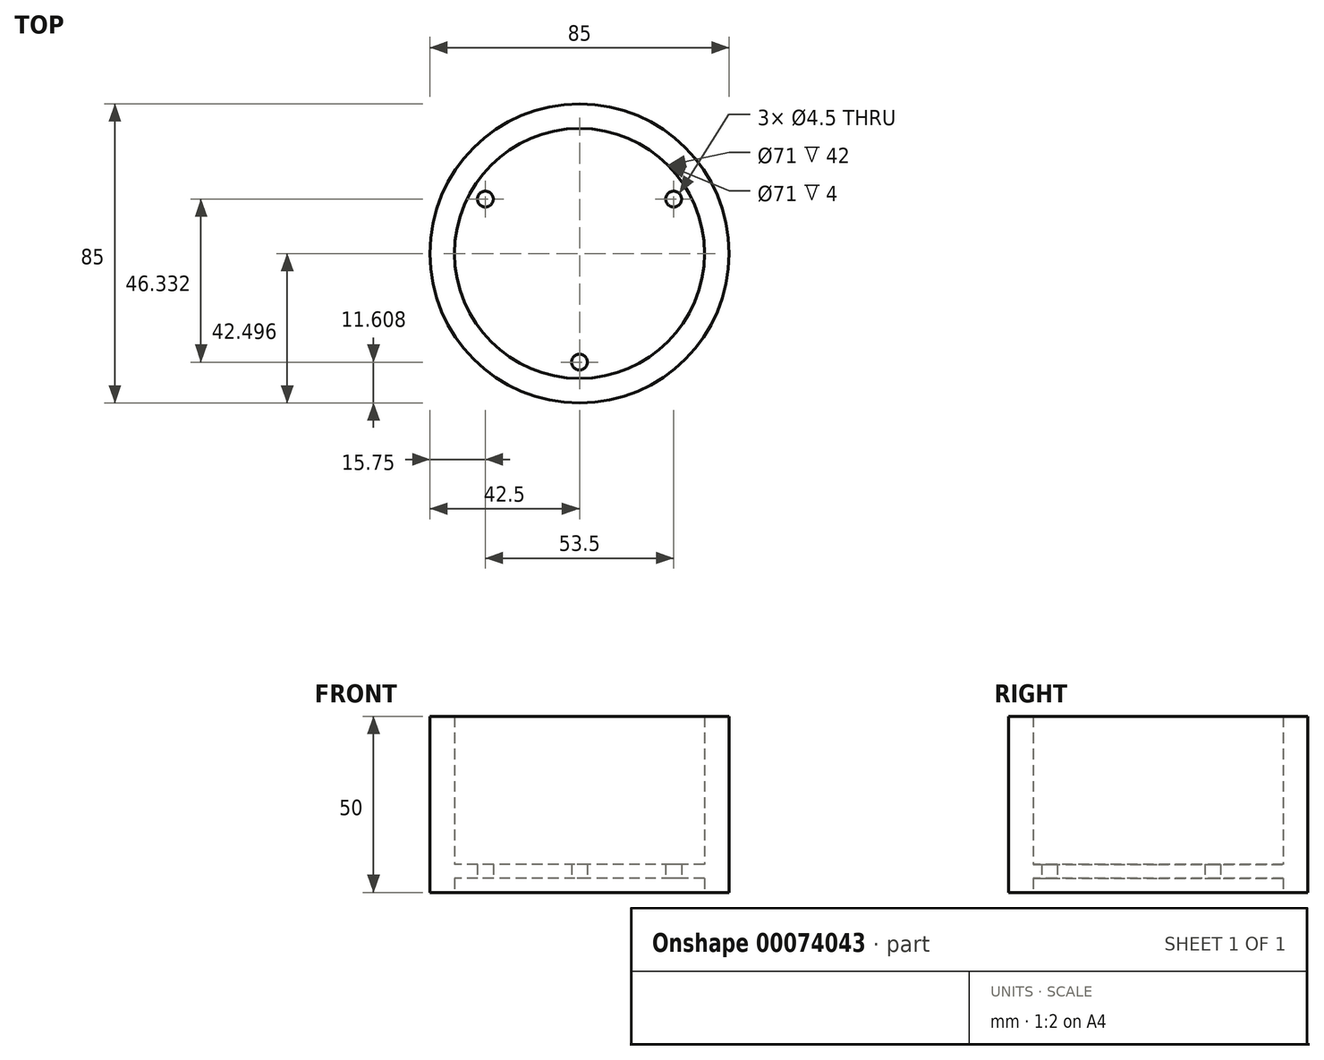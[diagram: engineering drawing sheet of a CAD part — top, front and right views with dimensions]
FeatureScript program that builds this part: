
annotation { "Feature Type Name" : "Feature", "Feature Type Description" : "" }
export const myFeature = defineFeature(function(context is Context, id is Id, definition is map)
    precondition{}
    {
        {
            var Q0;
            Q0=qCreatedBy(makeId("Top.planeOp"),FACE);
            var sketch = newSketch(context, id + "F0", { "sketchPlane" : qUnion([Q0])});
            skLineSegment(sketch, "E0", {"start": v(0, 0) * mm, "end": v(53.5, 0) * mm});
            skLineSegment(sketch, "E1", {"start": v(53.5, 0) * mm, "end": v(26.75, -46.33) * mm});
            skLineSegment(sketch, "E2", {"start": v(26.75, -46.33) * mm, "end": v(0, 0) * mm});
            skLineSegment(sketch, "E3", {"start": v(0, 0) * mm, "end": v(40.12, -23.17) * mm});
            skLineSegment(sketch, "E4", {"start": v(13.38, -23.17) * mm, "end": v(53.5, 0) * mm});
            skLineSegment(sketch, "E5", {"start": v(26.75, -46.33) * mm, "end": v(26.75, 0) * mm});
            skCircle(sketch, "E6", {"center": v(26.75, -15.44) * mm, "radius": 35.5 * mm});
            skCircle(sketch, "E7", {"center": v(26.75, -15.44) * mm, "radius": 42.5 * mm});
            skCircle(sketch, "E8", {"center": v(0, 0) * mm, "radius": 2.25 * mm});
            skCircle(sketch, "E9", {"center": v(53.5, 0) * mm, "radius": 2.25 * mm});
            skCircle(sketch, "E10", {"center": v(26.75, -46.33) * mm, "radius": 2.25 * mm});
            skSolve(sketch);
        }
        {
            var Q0;
            Q0=makeQuery(id+"F0.imprint","IMPRINT",FACE,{"disambiguationData":[TD([[makeQuery(id+"F0.imprint","IMPRINT",EDGE,{"derivedFrom":sQuery(id+"F0.wireOp",EDGE,"E6")}),-1.0]])]});
            var Q1;
            Q1=makeQuery(id+"F0.imprint","IMPRINT",FACE,{"disambiguationData":[TD([[makeQuery(id+"F0.imprint","IMPRINT",EDGE,{"derivedFrom":sQuery(id+"F0.wireOp",EDGE,"E6")}),1.0]])]});
            var Q2;
            {var subQ0=sQuery(id+"F0.wireOp",EDGE,"E4");var subQ1=sQuery(id+"F0.wireOp",EDGE,"E2");var subQ2=makeQuery(id+"F0.imprint","INTERSECT",VERTEX,{"derivedFrom":[subQ1,subQ0]});Q2=makeQuery(id+"F0.imprint","IMPRINT",FACE,{"disambiguationData":[TD([[makeQuery(id+"F0.imprint","IMPRINT",EDGE,{"disambiguationData":[TD([[subQ2,-1.0]])],"derivedFrom":subQ1}),-1.0]])]});}
            var Q3;
            {var subQ0=sQuery(id+"F0.wireOp",EDGE,"E4");var subQ1=sQuery(id+"F0.wireOp",EDGE,"E2");var subQ2=makeQuery(id+"F0.imprint","INTERSECT",VERTEX,{"derivedFrom":[subQ1,subQ0]});Q3=makeQuery(id+"F0.imprint","IMPRINT",FACE,{"disambiguationData":[TD([[makeQuery(id+"F0.imprint","IMPRINT",EDGE,{"disambiguationData":[TD([[subQ2,1.0]])],"derivedFrom":subQ1}),-1.0]])]});}
            var Q4;
            {var subQ0=sQuery(id+"F0.wireOp",EDGE,"E3");var subQ1=sQuery(id+"F0.wireOp",EDGE,"E1");var subQ2=makeQuery(id+"F0.imprint","INTERSECT",VERTEX,{"derivedFrom":[subQ1,subQ0]});Q4=makeQuery(id+"F0.imprint","IMPRINT",FACE,{"disambiguationData":[TD([[makeQuery(id+"F0.imprint","IMPRINT",EDGE,{"disambiguationData":[TD([[subQ2,-1.0]])],"derivedFrom":subQ1}),-1.0]])]});}
            var Q5;
            {var subQ0=sQuery(id+"F0.wireOp",EDGE,"E5");var subQ1=sQuery(id+"F0.wireOp",EDGE,"E0");var subQ2=makeQuery(id+"F0.imprint","INTERSECT",VERTEX,{"derivedFrom":[subQ1,subQ0]});Q5=makeQuery(id+"F0.imprint","IMPRINT",FACE,{"disambiguationData":[TD([[makeQuery(id+"F0.imprint","IMPRINT",EDGE,{"disambiguationData":[TD([[subQ2,1.0]])],"derivedFrom":subQ1}),-1.0]])]});}
            var Q6;
            {var subQ0=sQuery(id+"F0.wireOp",EDGE,"E3");var subQ1=sQuery(id+"F0.wireOp",EDGE,"E1");var subQ2=makeQuery(id+"F0.imprint","INTERSECT",VERTEX,{"derivedFrom":[subQ1,subQ0]});Q6=makeQuery(id+"F0.imprint","IMPRINT",FACE,{"disambiguationData":[TD([[makeQuery(id+"F0.imprint","IMPRINT",EDGE,{"disambiguationData":[TD([[subQ2,1.0]])],"derivedFrom":subQ1}),-1.0]])]});}
            var Q7;
            {var subQ0=sQuery(id+"F0.wireOp",EDGE,"E5");var subQ1=sQuery(id+"F0.wireOp",EDGE,"E0");var subQ2=makeQuery(id+"F0.imprint","INTERSECT",VERTEX,{"derivedFrom":[subQ1,subQ0]});Q7=makeQuery(id+"F0.imprint","IMPRINT",FACE,{"disambiguationData":[TD([[makeQuery(id+"F0.imprint","IMPRINT",EDGE,{"disambiguationData":[TD([[subQ2,-1.0]])],"derivedFrom":subQ1}),-1.0]])]});}
            extrude(context, id + "F1", {"entities" : qUnion([Q0, Q1, Q2, Q3, Q4, Q5, Q6, Q7]), "depth" : 8 * mm});
        }
        {
            var Q0;
            Q0=makeQuery(id+"F0.imprint","IMPRINT",FACE,{"disambiguationData":[TD([[makeQuery(id+"F0.imprint","IMPRINT",EDGE,{"derivedFrom":sQuery(id+"F0.wireOp",EDGE,"E6")}),-1.0]])]});
            extrude(context, id + "F2", {"entities" : qUnion([Q0]), "operationType" : NewBodyOperationType.ADD, "depth" : 50 * mm});
        }
        {
            var Q0;
            Q0=makeQuery(id+"F0.imprint","IMPRINT",FACE,{"disambiguationData":[TD([[makeQuery(id+"F0.imprint","IMPRINT",EDGE,{"derivedFrom":sQuery(id+"F0.wireOp",EDGE,"E6")}),1.0]])]});
            var Q1;
            {var subQ0=sQuery(id+"F0.wireOp",EDGE,"E5");var subQ1=sQuery(id+"F0.wireOp",EDGE,"E0");var subQ2=makeQuery(id+"F0.imprint","INTERSECT",VERTEX,{"derivedFrom":[subQ1,subQ0]});Q1=makeQuery(id+"F0.imprint","IMPRINT",FACE,{"disambiguationData":[TD([[makeQuery(id+"F0.imprint","IMPRINT",EDGE,{"disambiguationData":[TD([[subQ2,-1.0]])],"derivedFrom":subQ1}),-1.0]])]});}
            var Q2;
            {var subQ0=sQuery(id+"F0.wireOp",EDGE,"E5");var subQ1=sQuery(id+"F0.wireOp",EDGE,"E0");var subQ2=makeQuery(id+"F0.imprint","INTERSECT",VERTEX,{"derivedFrom":[subQ1,subQ0]});Q2=makeQuery(id+"F0.imprint","IMPRINT",FACE,{"disambiguationData":[TD([[makeQuery(id+"F0.imprint","IMPRINT",EDGE,{"disambiguationData":[TD([[subQ2,1.0]])],"derivedFrom":subQ1}),-1.0]])]});}
            var Q3;
            {var subQ0=sQuery(id+"F0.wireOp",EDGE,"E4");var subQ1=sQuery(id+"F0.wireOp",EDGE,"E2");var subQ2=makeQuery(id+"F0.imprint","INTERSECT",VERTEX,{"derivedFrom":[subQ1,subQ0]});Q3=makeQuery(id+"F0.imprint","IMPRINT",FACE,{"disambiguationData":[TD([[makeQuery(id+"F0.imprint","IMPRINT",EDGE,{"disambiguationData":[TD([[subQ2,-1.0]])],"derivedFrom":subQ1}),-1.0]])]});}
            var Q4;
            {var subQ0=sQuery(id+"F0.wireOp",EDGE,"E4");var subQ1=sQuery(id+"F0.wireOp",EDGE,"E2");var subQ2=makeQuery(id+"F0.imprint","INTERSECT",VERTEX,{"derivedFrom":[subQ1,subQ0]});Q4=makeQuery(id+"F0.imprint","IMPRINT",FACE,{"disambiguationData":[TD([[makeQuery(id+"F0.imprint","IMPRINT",EDGE,{"disambiguationData":[TD([[subQ2,1.0]])],"derivedFrom":subQ1}),-1.0]])]});}
            var Q5;
            {var subQ0=sQuery(id+"F0.wireOp",EDGE,"E3");var subQ1=sQuery(id+"F0.wireOp",EDGE,"E1");var subQ2=makeQuery(id+"F0.imprint","INTERSECT",VERTEX,{"derivedFrom":[subQ1,subQ0]});Q5=makeQuery(id+"F0.imprint","IMPRINT",FACE,{"disambiguationData":[TD([[makeQuery(id+"F0.imprint","IMPRINT",EDGE,{"disambiguationData":[TD([[subQ2,-1.0]])],"derivedFrom":subQ1}),-1.0]])]});}
            var Q6;
            {var subQ0=sQuery(id+"F0.wireOp",EDGE,"E3");var subQ1=sQuery(id+"F0.wireOp",EDGE,"E1");var subQ2=makeQuery(id+"F0.imprint","INTERSECT",VERTEX,{"derivedFrom":[subQ1,subQ0]});Q6=makeQuery(id+"F0.imprint","IMPRINT",FACE,{"disambiguationData":[TD([[makeQuery(id+"F0.imprint","IMPRINT",EDGE,{"disambiguationData":[TD([[subQ2,1.0]])],"derivedFrom":subQ1}),-1.0]])]});}
            extrude(context, id + "F3", {"entities" : qUnion([Q0, Q1, Q2, Q3, Q4, Q5, Q6]), "operationType" : NewBodyOperationType.REMOVE, "depth" : 4 * mm});
        }
    });
